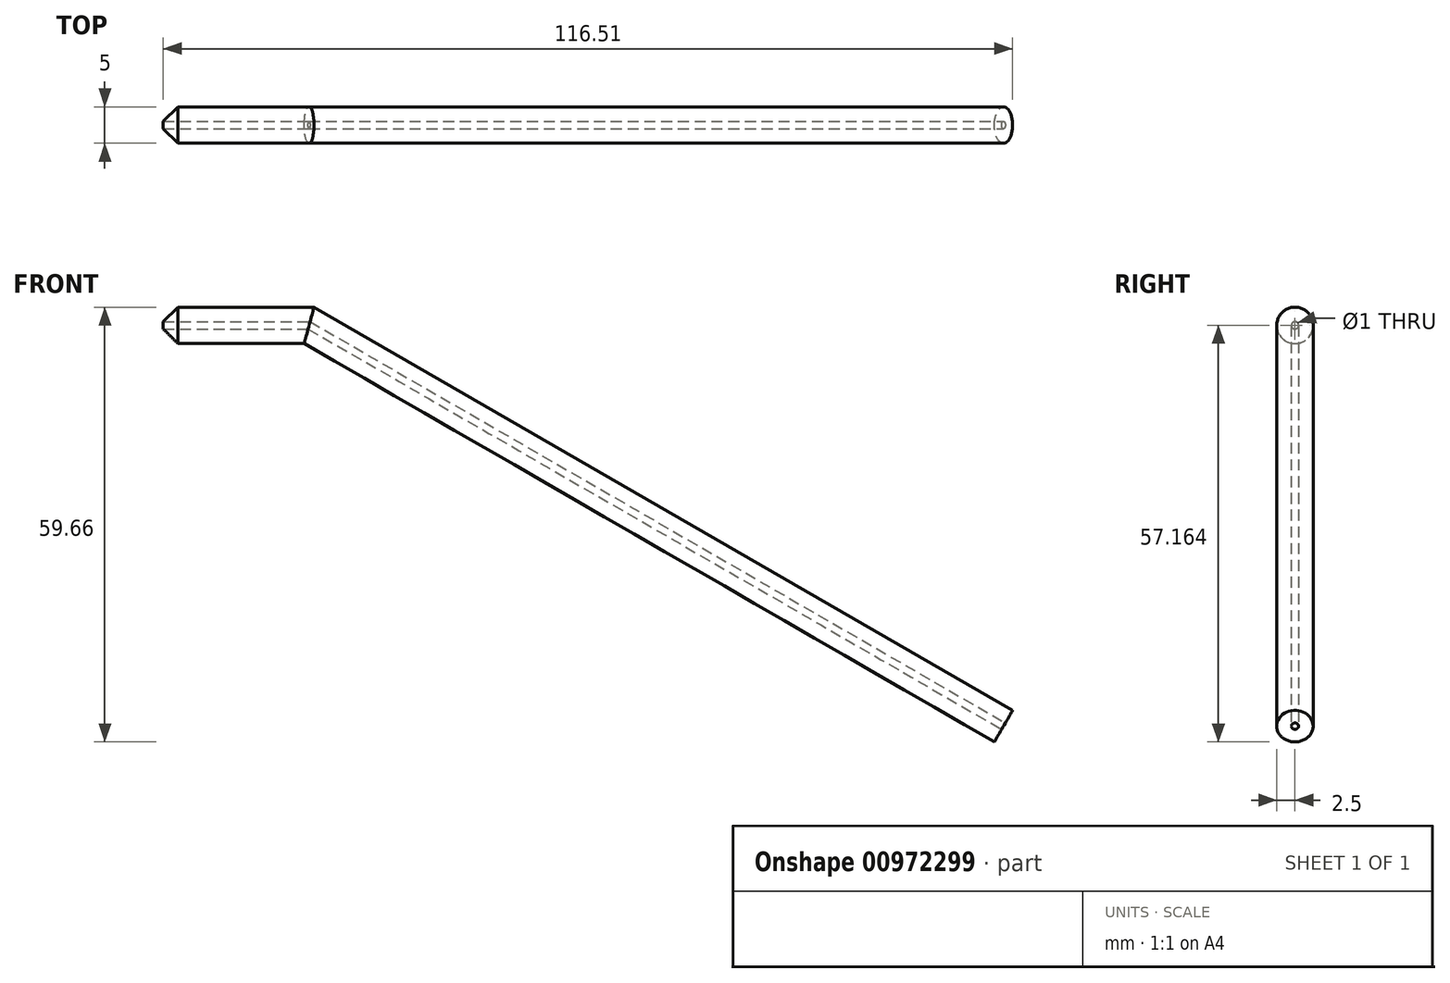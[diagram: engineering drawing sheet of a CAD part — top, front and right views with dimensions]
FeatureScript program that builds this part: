
annotation { "Feature Type Name" : "Feature", "Feature Type Description" : "" }
export const myFeature = defineFeature(function(context is Context, id is Id, definition is map)
    precondition{}
    {
        {
            var Q0;
            Q0=qCreatedBy(makeId("Front.planeOp"),FACE);
            var sketch = newSketch(context, id + "F0", { "sketchPlane" : qUnion([Q0])});
            skLineSegment(sketch, "E0", {"start": v(0, 40.14) * mm, "end": v(20, 40.14) * mm});
            skLineSegment(sketch, "E1", {"start": v(20, 40.14) * mm, "end": v(115.26, -14.86) * mm});
            skSolve(sketch);
        }
        {
            var Q0;
            Q0=qCreatedBy(makeId("Right.planeOp"),FACE);
            var sketch = newSketch(context, id + "F1", { "sketchPlane" : qUnion([Q0])});
            skCircle(sketch, "E2", {"center": v(0, 40.14) * mm, "radius": 2.5 * mm});
            skSolve(sketch);
        }
        {
            var Q0;
            Q0=makeQuery(id+"F1.imprint","IMPRINT",FACE,{"disambiguationData":[TD([[makeQuery(id+"F1.imprint","IMPRINT",EDGE,{"derivedFrom":sQuery(id+"F1.wireOp",EDGE,"E2")}),1.0]])]});
            var Q1;
            Q1=sQuery(id+"F0.wireOp",EDGE,"E0");
            var Q2;
            Q2=sQuery(id+"F0.wireOp",EDGE,"E1");
            sweep(context, id + "F2", {"profiles" : qUnion([Q0]), "path" : qUnion([Q1, Q2])});
        }
        {
            var Q0;
            Q0=makeQuery(id+"F2.opSweep","CAP_EDGE",EDGE,{"disambiguationData":[OSD([sQuery(id+"F0.wireOp",VERTEX,"E0.start"),sQuery(id+"F1.wireOp",EDGE,"E2")])],"isStart":true});
            chamfer(context, id + "F3", {"entities" : qUnion([Q0]), "width" : 2 * mm});
        }
        {
            var Q0;
            Q0=makeQuery(id+"F2.opSweep","CAP_FACE",FACE,{"disambiguationData":[OSD([sQuery(id+"F0.wireOp",VERTEX,"E0.start"),sQuery(id+"F1.wireOp",EDGE,"E2")])],"isStart":true});
            var Q1;
            Q1=sQuery(id+"F0.wireOp",EDGE,"E0");
            var Q2;
            Q2=sQuery(id+"F0.wireOp",EDGE,"E1");
            sweep(context, id + "F4", {"operationType" : NewBodyOperationType.REMOVE, "profiles" : qUnion([Q0]), "path" : qUnion([Q1, Q2])});
        }
    });
